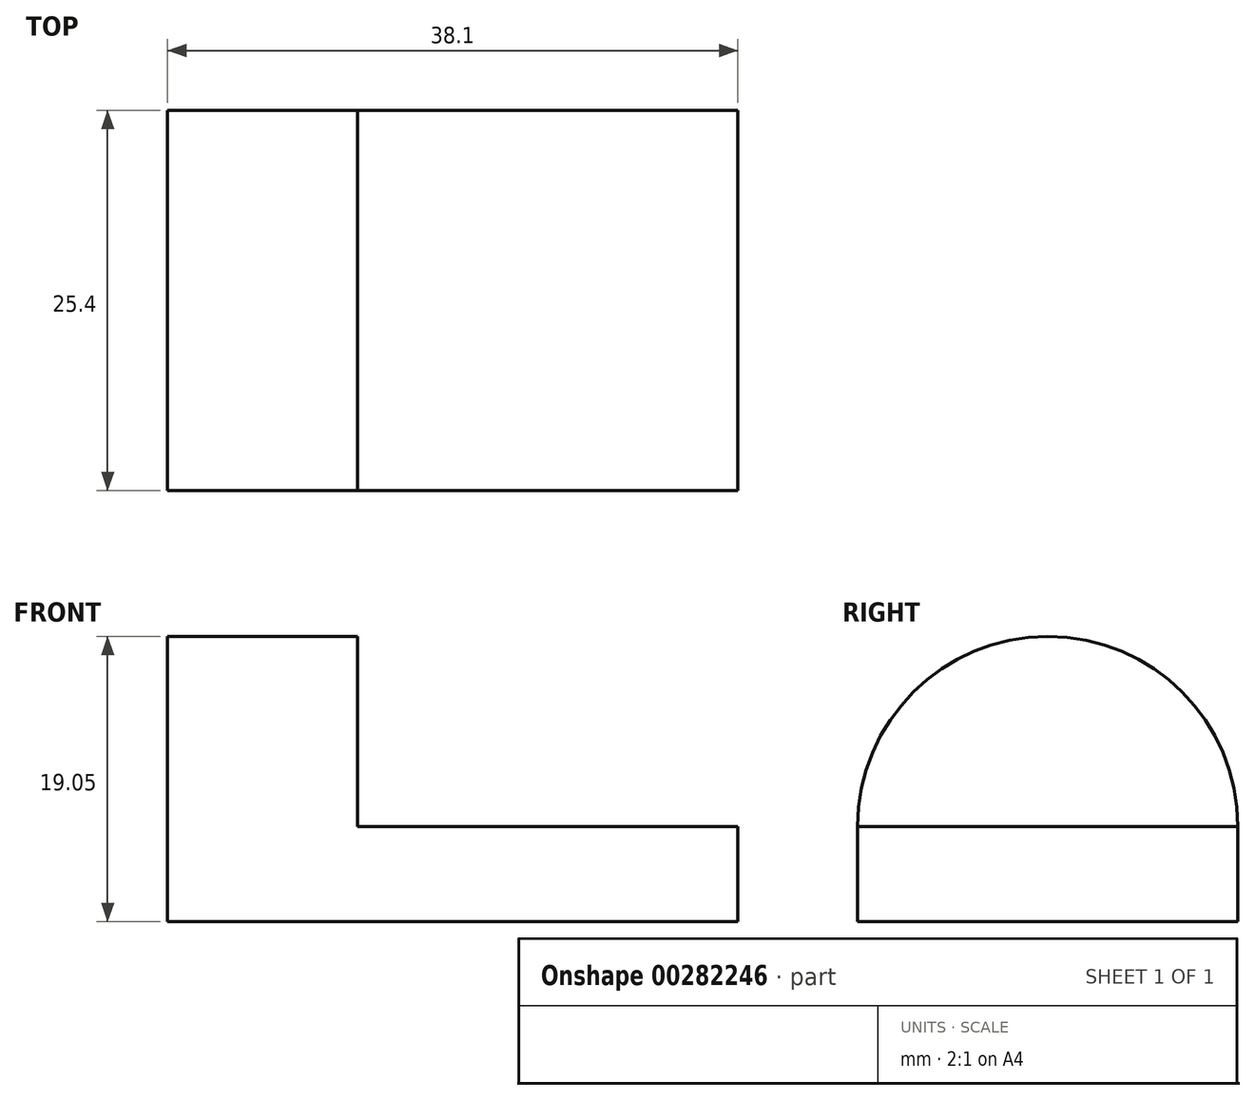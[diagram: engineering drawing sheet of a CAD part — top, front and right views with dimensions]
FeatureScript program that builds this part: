
annotation { "Feature Type Name" : "Feature", "Feature Type Description" : "" }
export const myFeature = defineFeature(function(context is Context, id is Id, definition is map)
    precondition{}
    {
        {
            var Q0;
            Q0=qCreatedBy(makeId("Top.planeOp"),FACE);
            var sketch = newSketch(context, id + "F0", { "sketchPlane" : qUnion([Q0])});
            skLineSegment(sketch, "E0.bottom", {"start": v(0, 0) * mm, "end": v(38.1, 0) * mm});
            skLineSegment(sketch, "E0.top", {"start": v(0, 25.4) * mm, "end": v(38.1, 25.4) * mm});
            skLineSegment(sketch, "E0.left", {"start": v(0, 0) * mm, "end": v(0, 25.4) * mm});
            skLineSegment(sketch, "E0.right", {"start": v(38.1, 0) * mm, "end": v(38.1, 25.4) * mm});
            skSolve(sketch);
        }
        {
            var Q0;
            Q0 = qSketchRegion(id + "F0", true);
            extrude(context, id + "F1", {"entities" : qUnion([Q0]), "depth" : 6.35 * mm});
        }
        {
            var Q0;
            Q0=makeQuery(id+"F1.opExtrude","SWEPT_FACE",FACE,{"disambiguationData":[OSD([sQuery(id+"F0.wireOp",EDGE,"E0.left")])]});
            var sketch = newSketch(context, id + "F2", { "sketchPlane" : qUnion([Q0])});
            skArc(sketch, "E1", {"start": v(0, 6.35) * mm, "mid": v(-12.7, 19.05) * mm, "end": v(-25.4, 6.35) * mm});
            skSolve(sketch);
        }
        {
            var Q0;
            Q0 = qSketchRegion(id + "F2", true);
            var Q1;
            Q1=makeQuery(id+"F2.imprint","IMPRINT",FACE,{"disambiguationData":[TD([[makeQuery(id+"F2.imprint","IMPRINT",EDGE,{"derivedFrom":sQuery(id+"F2.wireOp",EDGE,"E1")}),1.0]])]});
            extrude(context, id + "F3", {"entities" : qUnion([Q0, Q1]), "operationType" : NewBodyOperationType.ADD, "oppositeDirection" : true, "depth" : 12.7 * mm});
        }
    });
